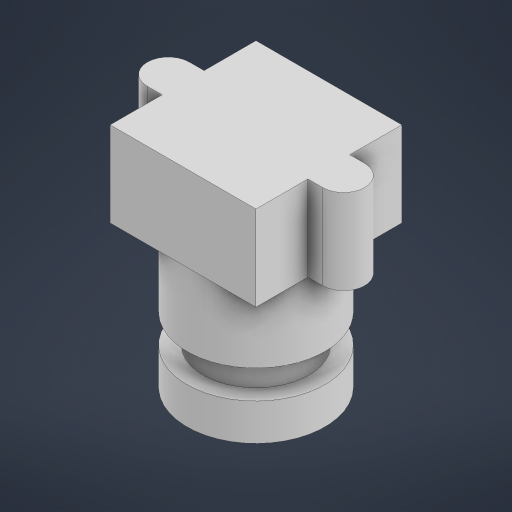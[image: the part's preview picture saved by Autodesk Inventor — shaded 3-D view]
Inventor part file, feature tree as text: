
AUTODESK INVENTOR PART (.ipt)
format: ipt  version: 2024 (Build 280153000, 153)  size: 216,576 bytes
history: native  units: mm
features: extrude x4, sketch x4, other x1
ambient origin geometry x8: Origin, YZ Plane, XZ Plane, XY Plane, X Axis, Y Axis, Z Axis, Center Point
bodies: Body1 (feature_tree)
feature tree (9):
  other  "Твердое тело1"
  extrude  "Выдавливание1"  Depth=4.7mm
  extrude  "Выдавливание2"  Depth=4.0mm
  extrude  "Выдавливание3"  Depth=16.3mm
  extrude  "Выдавливание4"  Depth=16.3mm
  sketch  "Эскиз1"
  sketch  "Эскиз2"
  sketch  "Эскиз3"
  sketch  "Эскиз4"
